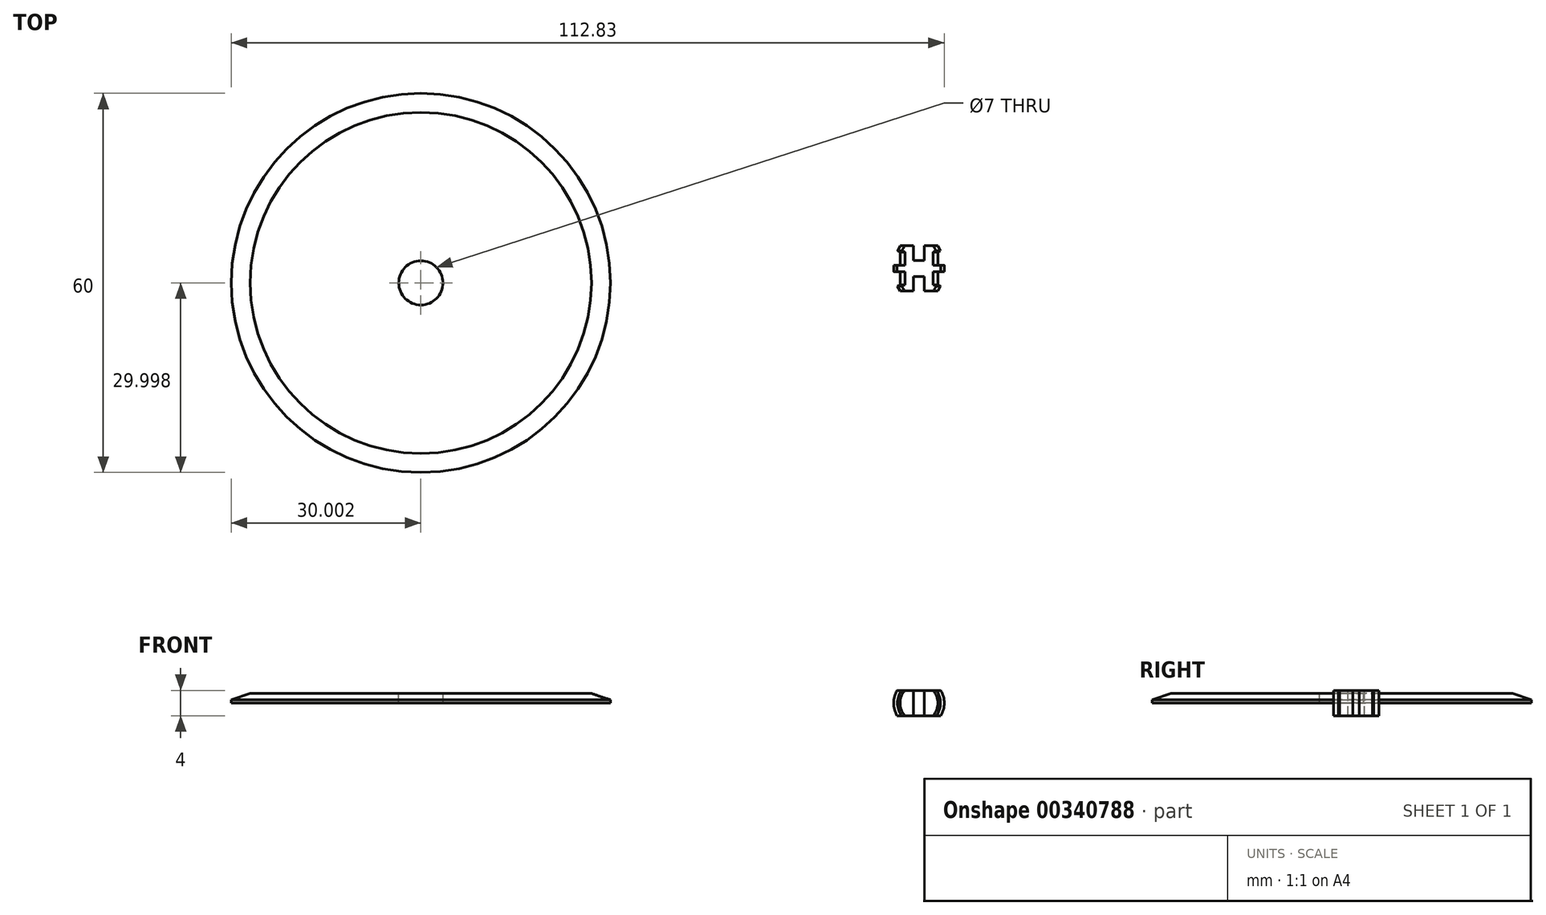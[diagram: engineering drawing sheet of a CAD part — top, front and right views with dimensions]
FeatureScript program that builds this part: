
annotation { "Feature Type Name" : "Feature", "Feature Type Description" : "" }
export const myFeature = defineFeature(function(context is Context, id is Id, definition is map)
    precondition{}
    {
        {
            assignVariable(context, id + "F0", {"name" : "wheelWidth", "anyValue" : 1.5});
        }
        {
            var Q0;
            Q0=qCreatedBy(makeId("Top.planeOp"),FACE);
            var sketch = newSketch(context, id + "F1", { "sketchPlane" : qUnion([Q0])});
            skCircle(sketch, "E0", {"center": v(-61.75, -31.08) * mm, "radius": 30 * mm});
            skSolve(sketch);
        }
        {
            var Q0;
            Q0 = qSketchRegion(id + "F1", true);
            extrude(context, id + "F2", {"entities" : qUnion([Q0]), "depth" : (getVariable(context, 'wheelWidth')) * mm});
        }
        {
            var Q0;
            Q0=makeQuery(id+"F2.opExtrude","CAP_FACE",FACE,{"disambiguationData":[OSD([sQuery(id+"F1.wireOp",EDGE,"E0")])],"isStart":false});
            var sketch = newSketch(context, id + "F3", { "sketchPlane" : qUnion([Q0])});
            skCircle(sketch, "E1", {"center": v(-61.75, -31.08) * mm, "radius": 3.5 * mm});
            skSolve(sketch);
        }
        {
            var Q0;
            Q0 = qSketchRegion(id + "F3", true);
            extrude(context, id + "F4", {"entities" : qUnion([Q0]), "operationType" : NewBodyOperationType.REMOVE, "oppositeDirection" : true, "depth" : 25 * mm});
        }
        {
            var Q0;
            Q0=makeQuery(id+"F2.opExtrude","CAP_EDGE",EDGE,{"disambiguationData":[OSD([sQuery(id+"F1.wireOp",EDGE,"E0")])],"isStart":false});
            chamfer(context, id + "F5", {"entities" : qUnion([Q0]), "chamferType" : ChamferType.TWO_OFFSETS, "width1" : (getVariable(context, 'wheelWidth') * 2) * mm, "oppositeDirection" : false, "width2" : (getVariable(context, 'wheelWidth') * 2 / 3) * mm, "tangentPropagation" : true});
        }
        {
            var Q0;
            Q0=qCreatedBy(makeId("Top.planeOp"),FACE);
            var sketch = newSketch(context, id + "F6", { "sketchPlane" : qUnion([Q0])});
            skLineSegment(sketch, "E2", {"start": v(13.72, -26) * mm, "end": v(14.08, -26.2) * mm});
            skLineSegment(sketch, "E3", {"start": v(14.08, -26.2) * mm, "end": v(14.08, -28.3) * mm});
            skLineSegment(sketch, "E4", {"start": v(14.08, -28.3) * mm, "end": v(13.08, -28.3) * mm});
            skLineSegment(sketch, "E5", {"start": v(13.08, -28.3) * mm, "end": v(13.08, -29.3) * mm});
            skLineSegment(sketch, "E6", {"start": v(13.08, -29.3) * mm, "end": v(14.08, -29.3) * mm});
            skLineSegment(sketch, "E7", {"start": v(14.08, -29.3) * mm, "end": v(14.08, -31.4) * mm});
            skLineSegment(sketch, "E8", {"start": v(14.08, -31.4) * mm, "end": v(13.68, -31.6) * mm});
            skLineSegment(sketch, "E9", {"start": v(13.68, -31.6) * mm, "end": v(14.08, -32.4) * mm});
            skLineSegment(sketch, "E10", {"start": v(14.08, -32.4) * mm, "end": v(17.08, -32.4) * mm});
            skLineSegment(sketch, "E11", {"start": v(17.08, -32.4) * mm, "end": v(17.08, -25.2) * mm});
            skLineSegment(sketch, "E12", {"start": v(17.08, -25.2) * mm, "end": v(14.08, -25.2) * mm});
            skLineSegment(sketch, "E13", {"start": v(14.08, -25.2) * mm, "end": v(13.72, -26) * mm});
            skSolve(sketch);
        }
        {
            var Q0;
            Q0 = qSketchRegion(id + "F6", true);
            var Q1;
            Q1=sQuery(id+"F6.wireOp",EDGE,"E11");
            revolve(context, id + "F7", {"entities" : qUnion([Q0]), "axis" : qUnion([Q1]), "revolveType" : RevolveType.FULL});
        }
        {
            var Q0;
            Q0=makeQuery(id+"F7.opRevolve","SWEPT_FACE",FACE,{"disambiguationData":[OSD([sQuery(id+"F6.wireOp",EDGE,"E10")])]});
            var sketch = newSketch(context, id + "F8", { "sketchPlane" : qUnion([Q0])});
            skLineSegment(sketch, "E14.bottom", {"start": v(21.08, -2) * mm, "end": v(13.08, -2) * mm});
            skLineSegment(sketch, "E14.top", {"start": v(21.08, 2) * mm, "end": v(13.08, 2) * mm});
            skLineSegment(sketch, "E14.left", {"start": v(21.08, -2) * mm, "end": v(21.08, 2) * mm});
            skLineSegment(sketch, "E14.right", {"start": v(13.08, -2) * mm, "end": v(13.08, 2) * mm});
            skPoint(sketch, "E14.middle", {"position": v(17.08, 0) * mm});
            skLineSegment(sketch, "E15.bottom", {"start": v(21.58, -4) * mm, "end": v(12.58, -4) * mm});
            skLineSegment(sketch, "E15.top", {"start": v(21.58, 4) * mm, "end": v(12.58, 4) * mm});
            skLineSegment(sketch, "E15.left", {"start": v(21.58, -4) * mm, "end": v(21.58, 4) * mm});
            skLineSegment(sketch, "E15.right", {"start": v(12.58, -4) * mm, "end": v(12.58, 4) * mm});
            skSolve(sketch);
        }
        {
            var Q0;
            Q0 = qSketchRegion(id + "F8", true);
            extrude(context, id + "F9", {"entities" : qUnion([Q0]), "operationType" : NewBodyOperationType.REMOVE, "oppositeDirection" : true, "depth" : 25 * mm});
        }
        {
            var Q0;
            Q0=makeQuery(id+"F9.boolean.opBoolean","COPY",FACE,{"derivedFrom":makeQuery(id+"F9.opExtrude","SWEPT_FACE",FACE,{"disambiguationData":[OSD([sQuery(id+"F8.wireOp",EDGE,"E14.top")])]})});
            var sketch = newSketch(context, id + "F10", { "sketchPlane" : qUnion([Q0])});
            skLineSegment(sketch, "E16.bottom", {"start": v(16.2, -25.2) * mm, "end": v(17.94, -25.2) * mm});
            skLineSegment(sketch, "E16.top", {"start": v(16.2, -27.51) * mm, "end": v(17.94, -27.51) * mm});
            skLineSegment(sketch, "E16.left", {"start": v(16.2, -25.2) * mm, "end": v(16.2, -27.51) * mm});
            skLineSegment(sketch, "E16.right", {"start": v(17.94, -25.2) * mm, "end": v(17.94, -27.51) * mm});
            skLineSegment(sketch, "E17.bottom", {"start": v(16.2, -32.4) * mm, "end": v(17.94, -32.4) * mm});
            skLineSegment(sketch, "E17.top", {"start": v(16.2, -30.07) * mm, "end": v(17.94, -30.07) * mm});
            skLineSegment(sketch, "E17.left", {"start": v(16.2, -32.4) * mm, "end": v(16.2, -30.07) * mm});
            skLineSegment(sketch, "E17.right", {"start": v(17.94, -32.4) * mm, "end": v(17.94, -30.07) * mm});
            skSolve(sketch);
        }
        {
            var Q0;
            Q0 = qSketchRegion(id + "F10", true);
            extrude(context, id + "F11", {"entities" : qUnion([Q0]), "operationType" : NewBodyOperationType.REMOVE, "oppositeDirection" : true, "depth" : 25 * mm});
        }
    });
